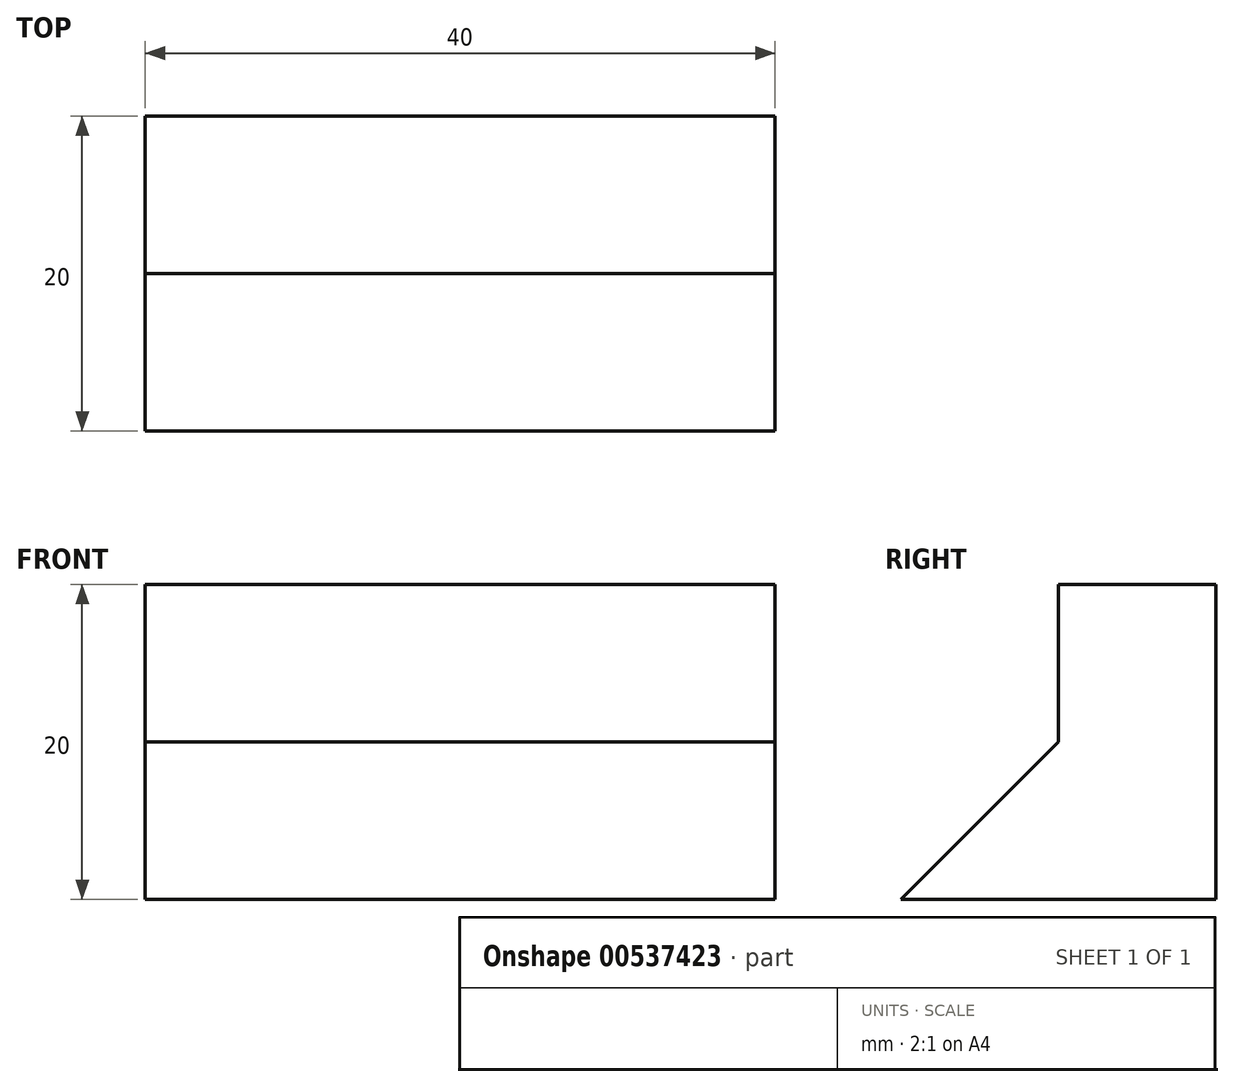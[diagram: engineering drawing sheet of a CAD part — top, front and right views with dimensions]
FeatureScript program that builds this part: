
annotation { "Feature Type Name" : "Feature", "Feature Type Description" : "" }
export const myFeature = defineFeature(function(context is Context, id is Id, definition is map)
    precondition{}
    {
        {
            var Q0;
            Q0=qCreatedBy(makeId("Top.planeOp"),FACE);
            var sketch = newSketch(context, id + "F0", { "sketchPlane" : qUnion([Q0])});
            skLineSegment(sketch, "E0.bottom", {"start": v(-61.8, -49.4) * mm, "end": v(-21.8, -49.4) * mm});
            skLineSegment(sketch, "E0.top", {"start": v(-61.8, -29.4) * mm, "end": v(-21.8, -29.4) * mm});
            skLineSegment(sketch, "E0.left", {"start": v(-61.8, -49.4) * mm, "end": v(-61.8, -29.4) * mm});
            skLineSegment(sketch, "E0.right", {"start": v(-21.8, -49.4) * mm, "end": v(-21.8, -29.4) * mm});
            skSolve(sketch);
        }
        {
            var Q0;
            Q0=makeQuery(id+"F0.imprint","IMPRINT",FACE,{"disambiguationData":[TD([[makeQuery(id+"F0.imprint","IMPRINT",EDGE,{"derivedFrom":sQuery(id+"F0.wireOp",EDGE,"E0.bottom")}),1.0]])]});
            extrude(context, id + "F1", {"entities" : qUnion([Q0]), "depth" : 20 * mm, "offsetDistance" : 25 * mm});
        }
        {
            var Q0;
            Q0=makeQuery(id+"F1.opExtrude","SWEPT_FACE",FACE,{"disambiguationData":[OSD([sQuery(id+"F0.wireOp",EDGE,"E0.right")])]});
            var sketch = newSketch(context, id + "F2", { "sketchPlane" : qUnion([Q0])});
            skLineSegment(sketch, "E1", {"start": v(-29.4, 20) * mm, "end": v(-30.28, 20) * mm});
            skLineSegment(sketch, "E2", {"start": v(-39.4, 20) * mm, "end": v(-39.4, 10) * mm});
            skPoint(sketch, "E2.endSnap0", {"position": v(-49.4, 10) * mm});
            skLineSegment(sketch, "E3", {"start": v(-39.4, 10) * mm, "end": v(-49.4, 0) * mm});
            skSolve(sketch);
        }
        {
            var Q0;
            {var subQ0=sQuery(id+"F2.wireOp",EDGE,"E2");Q0=makeQuery(id+"F2.imprint","IMPRINT",FACE,{"disambiguationData":[TD([[makeQuery(id+"F2.imprint","IMPRINT",EDGE,{"derivedFrom":subQ0}),-1.0]])]});}
            extrude(context, id + "F3", {"entities" : qUnion([Q0]), "operationType" : NewBodyOperationType.REMOVE, "endBound" : BoundingType.THROUGH_ALL, "oppositeDirection" : true, "depth" : 25 * mm, "offsetDistance" : 25 * mm});
        }
    });
